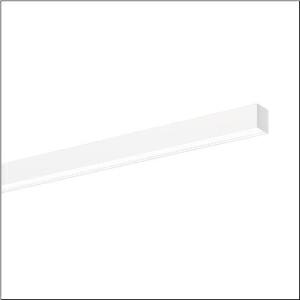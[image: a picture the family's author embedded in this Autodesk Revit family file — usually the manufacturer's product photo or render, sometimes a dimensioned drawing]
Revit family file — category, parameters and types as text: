
# Revit family: silica_r__21_51mx20tat2w_a418
name_source: partatom
category: Lighting Fixtures
units: mm (PartAtom-declared; Revit-internal decimal feet)

## family parameters
Cut with Voids When Loaded = No
Host = Face
Light Source = No
Part Type = Normal
Room Calculation Point = No
Round Connector Dimension = Use Diameter
Shared = No

## types (1)
- --- (1 x LED, 2400 lm, 20.5 W, 6500K)
    Apparent Load = 21 VA
    CIE Flux Codes = 48 79 96 100 100
    Color Rendering = 80
    Color Temperature = 6500K
    Default Elevation = 1800 mm
    Description = Silica® 21, office luminaire, primary optical cover: cover, of PMMA, opal, light emission: direct distribution, primary light characteristic: symmetric, installation type: surface-mounted, LED, rated luminous flux: 2.400lm, luminous efficacy: 112lm/W, light colour: 8tw, colour temperature: 2700..6500K, control gear: ECG DALI, with terminal, 3+2-pole, max. 2.5mm², mains connection: 220..240V, AC, 50/60Hz, rated input power: 21.5W, luminaire housing, of aluminium, traffic white (RAL 9016), length: 1.204mm, width: 53mm, height: 53mm, protection rating (complete): IP20, insulation class (complete): insulation class I (protective earthing), certification: CE, permissible operating ambient temperature: 0..+35°C, standard: EN 50419, packaging unit: 1 piece
    Height = 0 mm  [stored 0 ft]
    Lamp = 1 x LED
    Lamp Light Flux = 2400 lm
    Lamp Power = 20.5 W
    Lamp count = 1
    Length = 1204 mm
    Luminous efficacy = 117 lm/W
    Manufacturer = Siteco
    ModVariant = No
    Model = 51MX20TAT2W
    Mounting Place = Ceiling
    Mounting Type = Recessed
    Number of Poles = 1
    OnlyDefault = Yes
    Power Factor = 1
    Product Name = Silica® 21
    Product group = office luminaire | ceiling recessed
    ProductGroupID = 400
    Protection Class = Protection class I
    Protection Degree = IP 20
    RLX_Detail_Level = 1
    RLX_Emergency_Light_Flux = 0 lm
    RLX_Emergency_Type = 0
    RLX_Emergency_Type_DB = No
    RlxData = <blob elided: 20745 chars, md5=1bcb8744>
    Socket = socket
    Standby Power = 0 W
    System Light Flux = 2400 lm
    System Power = 21 W
    Type Comments = individual setting
    Type Image = l_1335877.jpg
    URL = http://relux.com
    VarID = @adj_109513
    Voltage = 0 V
    Weight = 0.00 kg
    Width = 53 mm

note: [stored X ft] marks values corroborated as IEEE doubles in the binary element streams (Revit-internal decimal feet)

## geometry (parser evidence)
native form markers: Blend x4, Sweep x10
no freeform markers — native parametric forms only
